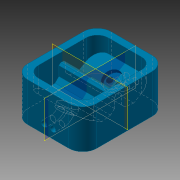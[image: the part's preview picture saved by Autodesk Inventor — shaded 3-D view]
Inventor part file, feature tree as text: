
AUTODESK INVENTOR PART (.ipt)
format: ipt  version: 2015 (Build 190159000, 159)  size: 183,808 bytes
history: native  units: in
note: dims shown in document units (in); Inventor stores cm internally (conversion verified against a paired STEP export)
features: sketch x5, other x3, plane x2
ambient origin geometry x8: Origin, YZ Plane, XZ Plane, XY Plane, X Axis, Y Axis, Z Axis, Center Point
bodies: Solid1 (feature_tree)
feature tree (10):
  other  "Line Tracker v3.ipt"
  other  "Solid1::Line Tracker v3.ipt"
  other  "TaggingFeature1"
  sketch  "Sketch1"  dims[d0=0.3937in]
  sketch  "Sketch2"
  sketch  "Sketch3"
  sketch  "Sketch4"
  sketch  "Sketch5"
  plane  "Work Plane1"
  plane  "Work Plane2"
